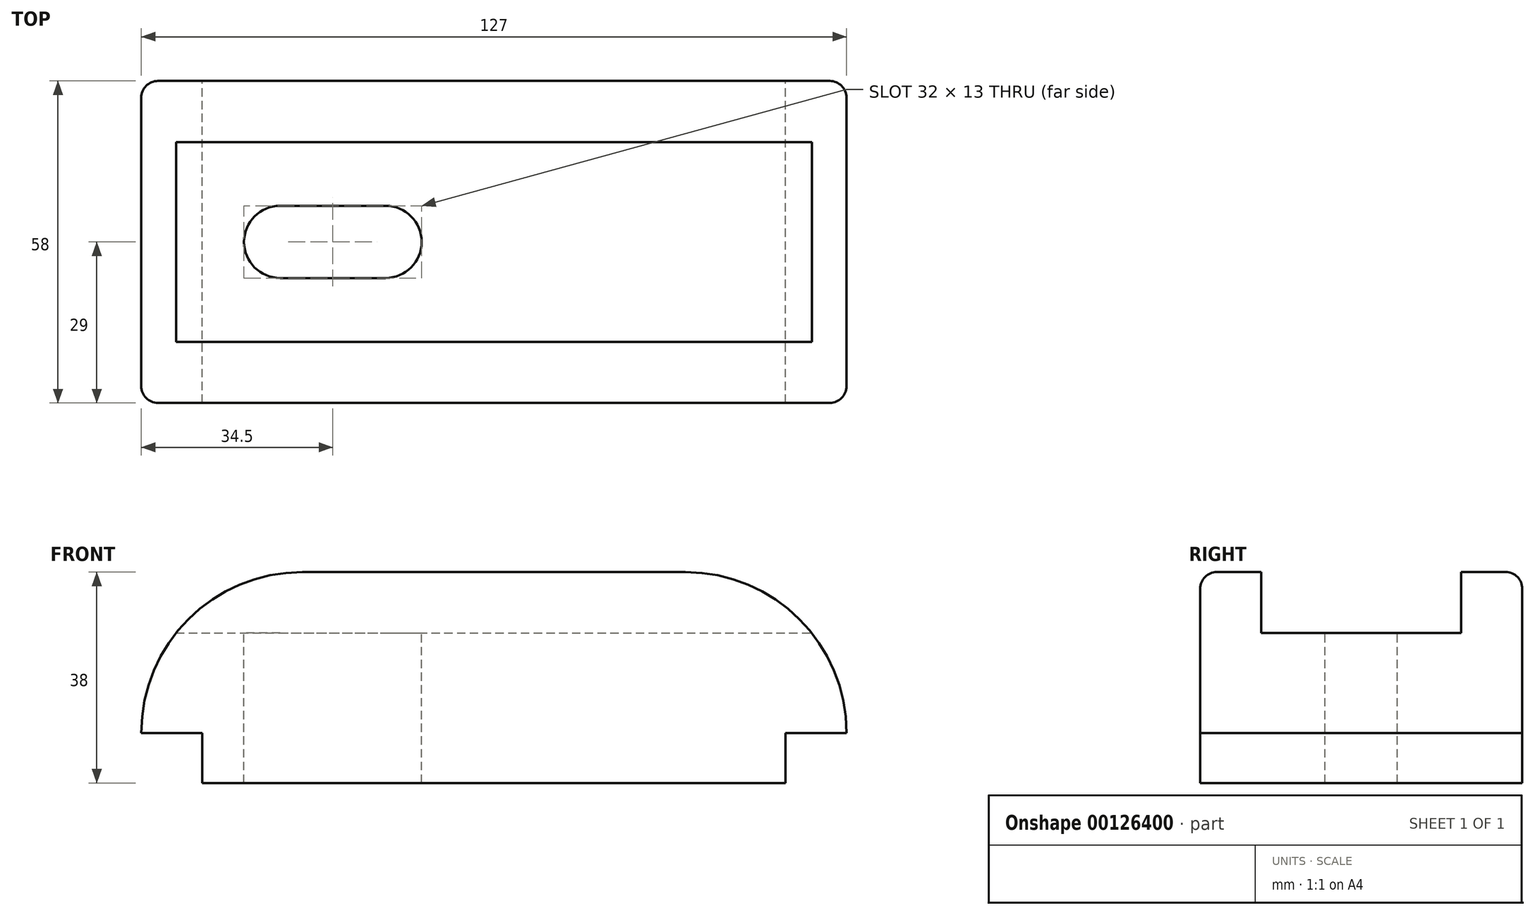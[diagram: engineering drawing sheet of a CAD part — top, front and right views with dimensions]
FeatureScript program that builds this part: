
annotation { "Feature Type Name" : "Feature", "Feature Type Description" : "" }
export const myFeature = defineFeature(function(context is Context, id is Id, definition is map)
    precondition{}
    {
        {
            var Q0;
            Q0=qCreatedBy(makeId("Front.planeOp"),FACE);
            var sketch = newSketch(context, id + "F0", { "sketchPlane" : qUnion([Q0])});
            skLineSegment(sketch, "E0", {"start": v(-52.5, 0) * mm, "end": v(0, 0) * mm});
            skLineSegment(sketch, "E1", {"start": v(0, 0) * mm, "end": v(52.5, 0) * mm});
            skLineSegment(sketch, "E2", {"start": v(52.5, 0) * mm, "end": v(52.5, 9) * mm});
            skLineSegment(sketch, "E3", {"start": v(52.5, 9) * mm, "end": v(63.5, 9) * mm});
            skLineSegment(sketch, "E4", {"start": v(-52.5, 0) * mm, "end": v(-52.5, 9) * mm});
            skLineSegment(sketch, "E5", {"start": v(-52.5, 9) * mm, "end": v(-63.5, 9) * mm});
            skArc(sketch, "E6", {"start": v(-63.5, 9) * mm, "mid": v(-55, 29.5) * mm, "end": v(-34.5, 38) * mm});
            skArc(sketch, "E7", {"start": v(63.5, 9) * mm, "mid": v(55, 29.5) * mm, "end": v(34.5, 38) * mm});
            skLineSegment(sketch, "E8", {"start": v(34.5, 38) * mm, "end": v(-34.5, 38) * mm});
            skSolve(sketch);
        }
        {
            var Q0;
            Q0 = qSketchRegion(id + "F0", true);
            extrude(context, id + "F1", {"entities" : qUnion([Q0]), "endBound" : BoundingType.SYMMETRIC, "depth" : 58 * mm});
        }
        {
            var Q0;
            Q0=qCreatedBy(makeId("Right.planeOp"),FACE);
            var sketch = newSketch(context, id + "F2", { "sketchPlane" : qUnion([Q0])});
            skLineSegment(sketch, "E9.bottom", {"start": v(18, 38) * mm, "end": v(-18, 38) * mm});
            skLineSegment(sketch, "E9.top", {"start": v(18, 27) * mm, "end": v(-18, 27) * mm});
            skLineSegment(sketch, "E9.left", {"start": v(18, 38) * mm, "end": v(18, 27) * mm});
            skLineSegment(sketch, "E9.right", {"start": v(-18, 38) * mm, "end": v(-18, 27) * mm});
            skPoint(sketch, "E9.middle", {"position": v(0, 32.5) * mm});
            skSolve(sketch);
        }
        {
            var Q0;
            Q0 = qSketchRegion(id + "F2", true);
            extrude(context, id + "F3", {"entities" : qUnion([Q0]), "operationType" : NewBodyOperationType.REMOVE, "endBound" : BoundingType.SYMMETRIC, "oppositeDirection" : true, "depth" : 127 * mm});
        }
        {
            var Q0;
            Q0=makeQuery(id+"F3.boolean.opBoolean","COPY",FACE,{"derivedFrom":makeQuery(id+"F3.opExtrude","SWEPT_FACE",FACE,{"disambiguationData":[OSD([sQuery(id+"F2.wireOp",EDGE,"E9.top")])]})});
            var sketch = newSketch(context, id + "F4", { "sketchPlane" : qUnion([Q0])});
            skLineSegment(sketch, "E10", {"start": v(-63.5, 0) * mm, "end": v(-38.5, 0) * mm, "construction": true});
            skArc(sketch, "E11", {"start": v(-38.5, -6.5) * mm, "mid": v(-45, 0) * mm, "end": v(-38.5, 6.5) * mm});
            skLineSegment(sketch, "E12", {"start": v(-38.5, 0) * mm, "end": v(-19.5, 0) * mm, "construction": true});
            skArc(sketch, "E13", {"start": v(-19.5, 6.5) * mm, "mid": v(-13, 0) * mm, "end": v(-19.5, -6.5) * mm});
            skLineSegment(sketch, "E14", {"start": v(-19.5, 6.5) * mm, "end": v(-38.5, 6.5) * mm});
            skLineSegment(sketch, "E15", {"start": v(-38.5, -6.5) * mm, "end": v(-19.5, -6.5) * mm});
            skSolve(sketch);
        }
        {
            var Q0;
            Q0 = qSketchRegion(id + "F4", true);
            var Q1;
            Q1 = qConstructionFilter(qBodyType(qCreatedBy(id + "F4" ,EDGE), BodyType.WIRE), ConstructionObject.NO);
            extrude(context, id + "F5", {"entities" : qUnion([Q0]), "operationType" : NewBodyOperationType.REMOVE, "surfaceEntities" : qUnion([Q1]), "endBound" : BoundingType.THROUGH_ALL, "oppositeDirection" : true, "depth" : 25 * mm});
        }
        {
            var Q0;
            Q0=makeQuery(id+"F1.opExtrude","CAP_EDGE",EDGE,{"disambiguationData":[OSD([sQuery(id+"F0.wireOp",EDGE,"E6")])],"isStart":false});
            var Q1;
            Q1=makeQuery(id+"F1.opExtrude","CAP_EDGE",EDGE,{"disambiguationData":[OSD([sQuery(id+"F0.wireOp",EDGE,"E7")])],"isStart":true});
            fillet(context, id + "F6", {"entities" : qUnion([Q0, Q1]), "radius" : 3 * mm, "tangentPropagation" : true, "allowEdgeOverflow" : false});
        }
    });
